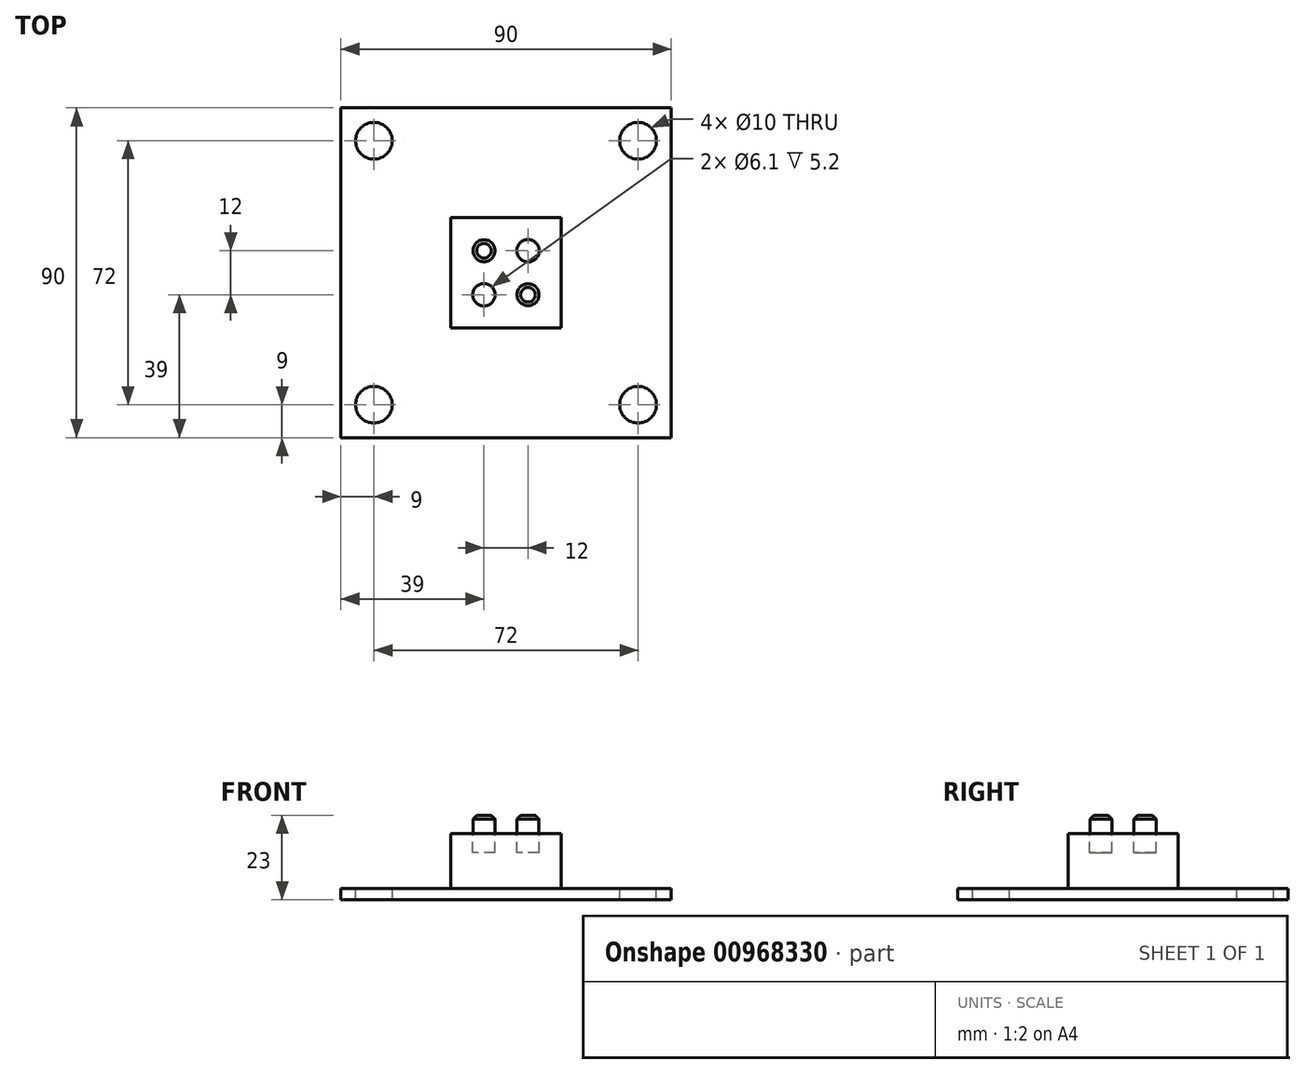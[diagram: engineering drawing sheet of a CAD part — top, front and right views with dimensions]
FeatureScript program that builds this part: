
annotation { "Feature Type Name" : "Feature", "Feature Type Description" : "" }
export const myFeature = defineFeature(function(context is Context, id is Id, definition is map)
    precondition{}
    {
        {
            var Q0;
            Q0=qCreatedBy(makeId("Top.planeOp"),FACE);
            var sketch = newSketch(context, id + "F0", { "sketchPlane" : qUnion([Q0])});
            skLineSegment(sketch, "E0.bottom", {"start": v(15, -15) * mm, "end": v(-15, -15) * mm});
            skLineSegment(sketch, "E0.top", {"start": v(15, 15) * mm, "end": v(-15, 15) * mm});
            skLineSegment(sketch, "E0.left", {"start": v(15, -15) * mm, "end": v(15, 15) * mm});
            skLineSegment(sketch, "E0.right", {"start": v(-15, -15) * mm, "end": v(-15, 15) * mm});
            skPoint(sketch, "E0.middle", {"position": v(0, 0) * mm});
            skSolve(sketch);
        }
        {
            var Q0;
            Q0 = qSketchRegion(id + "F0", true);
            extrude(context, id + "F1", {"entities" : qUnion([Q0]), "depth" : 15 * mm, "offsetDistance" : 25 * mm});
        }
        {
            var Q0;
            Q0=qCreatedBy(makeId("Top.planeOp"),FACE);
            var sketch = newSketch(context, id + "F2", { "sketchPlane" : qUnion([Q0])});
            skLineSegment(sketch, "E1.bottom", {"start": v(45, -45) * mm, "end": v(-45, -45) * mm});
            skLineSegment(sketch, "E1.top", {"start": v(45, 45) * mm, "end": v(-45, 45) * mm});
            skLineSegment(sketch, "E1.left", {"start": v(45, -45) * mm, "end": v(45, 45) * mm});
            skLineSegment(sketch, "E1.right", {"start": v(-45, -45) * mm, "end": v(-45, 45) * mm});
            skPoint(sketch, "E1.middle", {"position": v(0, 0) * mm});
            skSolve(sketch);
        }
        {
            var Q0;
            Q0 = qSketchRegion(id + "F2", true);
            extrude(context, id + "F3", {"entities" : qUnion([Q0]), "operationType" : NewBodyOperationType.ADD, "oppositeDirection" : true, "depth" : 3 * mm, "offsetDistance" : 25 * mm});
        }
        {
            var Q0;
            Q0=makeQuery(id+"F3.opExtrude","CAP_FACE",FACE,{"disambiguationData":[OSD([sQuery(id+"F2.wireOp",EDGE,"E1.bottom"),sQuery(id+"F2.wireOp",EDGE,"E1.top"),sQuery(id+"F2.wireOp",EDGE,"E1.left"),sQuery(id+"F2.wireOp",EDGE,"E1.right")])],"isStart":true});
            var sketch = newSketch(context, id + "F4", { "sketchPlane" : qUnion([Q0])});
            skCircle(sketch, "E2", {"center": v(-36, 36) * mm, "radius": 5 * mm});
            skCircle(sketch, "E3", {"center": v(36, 36) * mm, "radius": 5 * mm});
            skCircle(sketch, "E4", {"center": v(36, -36) * mm, "radius": 5 * mm});
            skCircle(sketch, "E5", {"center": v(-36, -36) * mm, "radius": 5 * mm});
            skSolve(sketch);
        }
        {
            var Q0;
            Q0 = qSketchRegion(id + "F4", true);
            extrude(context, id + "F5", {"entities" : qUnion([Q0]), "operationType" : NewBodyOperationType.REMOVE, "endBound" : BoundingType.THROUGH_ALL, "oppositeDirection" : true, "depth" : 25 * mm, "offsetDistance" : 25 * mm});
        }
        {
            var Q0;
            Q0=makeQuery(id+"F1.opExtrude","CAP_FACE",FACE,{"disambiguationData":[OSD([sQuery(id+"F0.wireOp",EDGE,"E0.bottom"),sQuery(id+"F0.wireOp",EDGE,"E0.top"),sQuery(id+"F0.wireOp",EDGE,"E0.left"),sQuery(id+"F0.wireOp",EDGE,"E0.right")])],"isStart":false});
            var sketch = newSketch(context, id + "F6", { "sketchPlane" : qUnion([Q0])});
            skCircle(sketch, "E6", {"center": v(-6, 6) * mm, "radius": 3 * mm});
            skCircle(sketch, "E7", {"center": v(6, -6) * mm, "radius": 3 * mm});
            skSolve(sketch);
        }
        {
            var Q0;
            Q0 = qSketchRegion(id + "F6", true);
            extrude(context, id + "F7", {"entities" : qUnion([Q0]), "operationType" : NewBodyOperationType.ADD, "depth" : 5 * mm, "offsetDistance" : 25 * mm});
        }
        {
            var Q0;
            Q0=makeQuery(id+"F7.opExtrude","CAP_EDGE",EDGE,{"disambiguationData":[OSD([sQuery(id+"F6.wireOp",EDGE,"E6")])],"isStart":false});
            var Q1;
            Q1=makeQuery(id+"F7.opExtrude","CAP_EDGE",EDGE,{"disambiguationData":[OSD([sQuery(id+"F6.wireOp",EDGE,"E7")])],"isStart":false});
            chamfer(context, id + "F8", {"entities" : qUnion([Q0, Q1]), "width" : 1 * mm, "tangentPropagation" : true});
        }
        {
            var Q0;
            Q0=makeQuery(id+"F1.opExtrude","CAP_FACE",FACE,{"disambiguationData":[OSD([sQuery(id+"F0.wireOp",EDGE,"E0.bottom"),sQuery(id+"F0.wireOp",EDGE,"E0.top"),sQuery(id+"F0.wireOp",EDGE,"E0.left"),sQuery(id+"F0.wireOp",EDGE,"E0.right")])],"isStart":false});
            var sketch = newSketch(context, id + "F9", { "sketchPlane" : qUnion([Q0])});
            skCircle(sketch, "E8", {"center": v(-6, -6) * mm, "radius": 3.05 * mm});
            skCircle(sketch, "E9", {"center": v(6, 6) * mm, "radius": 3.05 * mm});
            skSolve(sketch);
        }
        {
            var Q0;
            Q0 = qSketchRegion(id + "F9", true);
            extrude(context, id + "F10", {"entities" : qUnion([Q0]), "operationType" : NewBodyOperationType.REMOVE, "oppositeDirection" : true, "depth" : 5.2 * mm, "offsetDistance" : 25 * mm});
        }
    });
